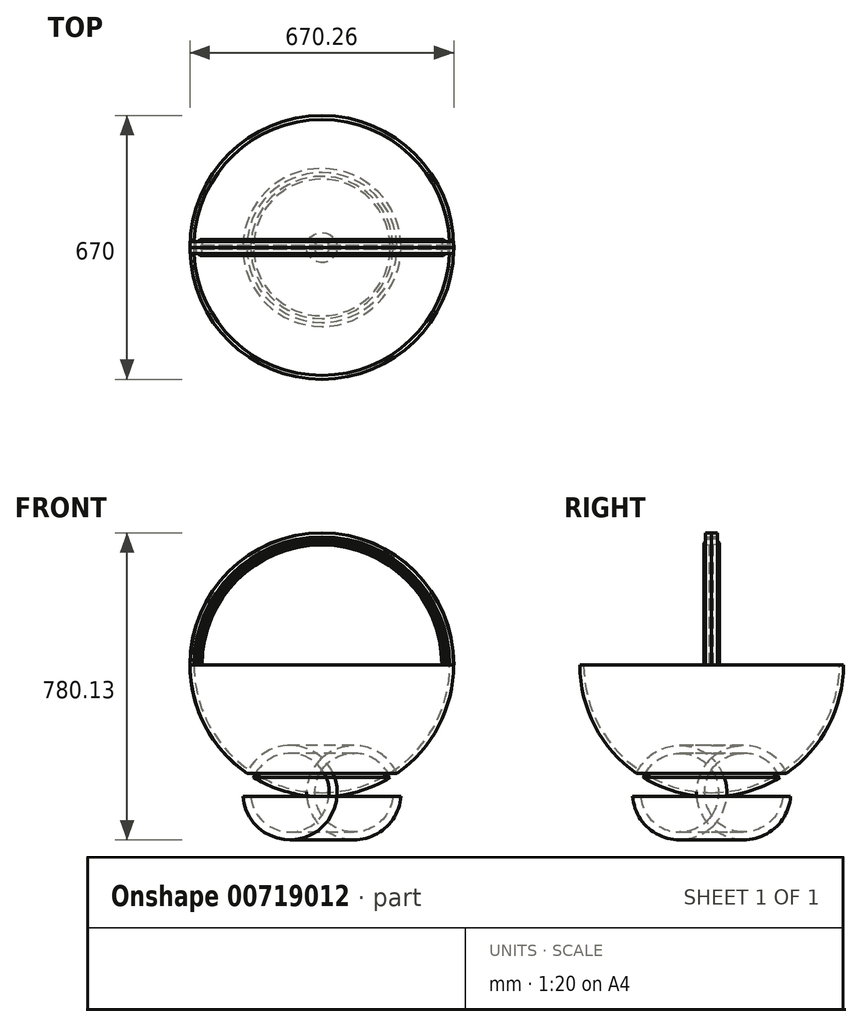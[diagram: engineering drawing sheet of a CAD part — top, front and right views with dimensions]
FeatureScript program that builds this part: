
annotation { "Feature Type Name" : "Feature", "Feature Type Description" : "" }
export const myFeature = defineFeature(function(context is Context, id is Id, definition is map)
    precondition{}
    {
        {
            var Q0;
            Q0=qCreatedBy(makeId("Front.planeOp"),FACE);
            var sketch = newSketch(context, id + "F0", { "sketchPlane" : qUnion([Q0])});
            skLineSegment(sketch, "E0", {"start": v(0, 0) * mm, "end": v(0, 325) * mm, "construction": true});
            skArc(sketch, "E1", {"start": v(0, 0) * mm, "mid": v(229.8, 95.2) * mm, "end": v(325, 325) * mm});
            skArc(sketch, "E2.0", {"start": v(0, -10) * mm, "mid": v(90.1, 2.34) * mm, "end": v(173.55, 38.46) * mm});
            skLineSegment(sketch, "E3", {"start": v(325, 325) * mm, "end": v(335, 325) * mm});
            skLineSegment(sketch, "E4", {"start": v(0, -10) * mm, "end": v(0, 0) * mm});
            skLineSegment(sketch, "E5", {"start": v(0, -10) * mm, "end": v(342.24, -10) * mm, "construction": true});
            skArc(sketch, "E6", {"start": v(180.74, -10) * mm, "mid": v(180.16, 14.68) * mm, "end": v(173.55, 38.46) * mm});
            skArc(sketch, "E7.0", {"start": v(200.82, -10) * mm, "mid": v(199.5, 20.4) * mm, "end": v(190.56, 49.48) * mm});
            skArc(sketch, "E8.trimOffspring", {"start": v(190.56, 49.48) * mm, "mid": v(296.7, 169.46) * mm, "end": v(335, 325) * mm});
            skLineSegment(sketch, "E9", {"start": v(180.74, -10) * mm, "end": v(200.82, -10) * mm});
            skSolve(sketch);
        }
        {
            var Q0;
            Q0=makeQuery(id+"F0.imprint","IMPRINT",FACE,{"disambiguationData":[TD([[makeQuery(id+"F0.imprint","IMPRINT",EDGE,{"derivedFrom":sQuery(id+"F0.wireOp",EDGE,"E1")}),-1.0]])]});
            var Q1;
            Q1=sQuery(id+"F0.wireOp",EDGE,"E0");
            revolve(context, id + "F1", {"surfaceOperationType" : NewSurfaceOperationType.NEW, "entities" : qUnion([Q0]), "axis" : qUnion([Q1]), "revolveType" : RevolveType.FULL});
        }
        {
            var Q0;
            Q0=qCreatedBy(makeId("Front.planeOp"),FACE);
            var sketch = newSketch(context, id + "F2", { "sketchPlane" : qUnion([Q0])});
            skArc(sketch, "E10", {"start": v(335, 325) * mm, "mid": v(0, 660) * mm, "end": v(-335, 325) * mm});
            skLineSegment(sketch, "E11", {"start": v(0, 325) * mm, "end": v(335, 325) * mm, "construction": true});
            skLineSegment(sketch, "E12", {"start": v(0, 325) * mm, "end": v(-335, 325) * mm, "construction": true});
            skSolve(sketch);
        }
        {
            var Q0;
            Q0=makeQuery(id+"F1.opRevolve","SWEPT_FACE",FACE,{"disambiguationData":[OSD([sQuery(id+"F0.wireOp",EDGE,"E3")])]});
            cPlane(context, id + "F3", {"entities" : qUnion([Q0]), "cplaneType" : CPlaneType.OFFSET, "offset" : 0 * mm, "width" : 150 * mm, "height" : 150 * mm});
        }
        {
            var Q0;
            Q0=qCreatedBy(id+"F3.planeOp",FACE);
            var sketch = newSketch(context, id + "F4", { "sketchPlane" : qUnion([Q0])});
            skLineSegment(sketch, "E13", {"start": v(335.13, 0) * mm, "end": v(334.66, -15) * mm});
            skLineSegment(sketch, "E14", {"start": v(334.66, -15) * mm, "end": v(324.65, -15) * mm});
            skLineSegment(sketch, "E15", {"start": v(324.65, -15) * mm, "end": v(324.96, -5) * mm});
            skLineSegment(sketch, "E16", {"start": v(324.96, -5) * mm, "end": v(319.86, -5) * mm});
            skLineSegment(sketch, "E17", {"start": v(319.86, -5) * mm, "end": v(319.55, -15) * mm});
            skLineSegment(sketch, "E18", {"start": v(319.55, -15) * mm, "end": v(314.55, -15) * mm});
            skLineSegment(sketch, "E19", {"start": v(314.55, -15) * mm, "end": v(309.55, -20) * mm});
            skLineSegment(sketch, "E20", {"start": v(309.55, -20) * mm, "end": v(304.54, -15) * mm});
            skLineSegment(sketch, "E21", {"start": v(304.54, -15) * mm, "end": v(305, 0) * mm});
            skLineSegment(sketch, "E22.MirrorCS", {"start": v(324.65, 15) * mm, "end": v(324.96, 5) * mm});
            skLineSegment(sketch, "E23.MirrorCS", {"start": v(334.66, 15) * mm, "end": v(324.65, 15) * mm});
            skLineSegment(sketch, "E24.MirrorCS", {"start": v(324.96, 5) * mm, "end": v(319.86, 5) * mm});
            skLineSegment(sketch, "E25.MirrorCS", {"start": v(319.55, 15) * mm, "end": v(314.55, 15) * mm});
            skLineSegment(sketch, "E26.MirrorCS", {"start": v(335.13, 0) * mm, "end": v(334.66, 15) * mm});
            skLineSegment(sketch, "E27.MirrorCS", {"start": v(304.54, 15) * mm, "end": v(305, 0) * mm});
            skLineSegment(sketch, "E28.MirrorCS", {"start": v(309.55, 20) * mm, "end": v(304.54, 15) * mm});
            skLineSegment(sketch, "E29.MirrorCS", {"start": v(314.55, 15) * mm, "end": v(309.55, 20) * mm});
            skLineSegment(sketch, "E30.MirrorCS", {"start": v(319.86, 5) * mm, "end": v(319.55, 15) * mm});
            skSolve(sketch);
        }
        {
            var Q0;
            Q0 = qSketchRegion(id + "F4", true);
            var Q1;
            Q1=sQuery(id+"F2.wireOp",EDGE,"E10");
            sweep(context, id + "F5", {"profiles" : qUnion([Q0]), "path" : qUnion([Q1])});
        }
    });
